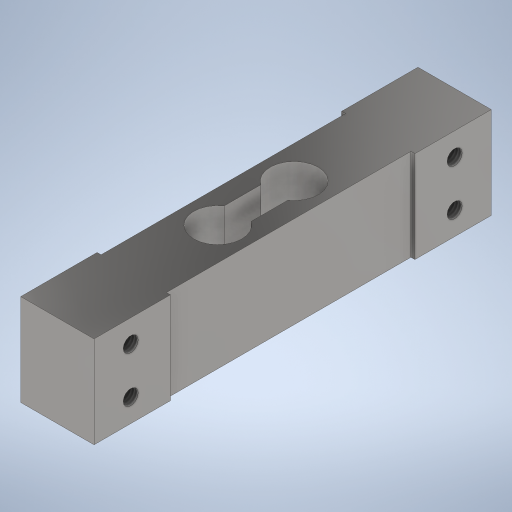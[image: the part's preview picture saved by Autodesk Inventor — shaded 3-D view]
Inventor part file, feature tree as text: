
AUTODESK INVENTOR PART (.ipt)
format: ipt  version: 2023.2 (Build 272271030, 271C)  size: 306,176 bytes
history: native  units: mm
features: sketch x2, other x1, extrude x1, hole x1
ambient origin geometry x8: Origin, YZ Plane, XZ Plane, XY Plane, X Axis, Y Axis, Z Axis, Center Point
bodies: Body1 (feature_tree)
feature tree (5):
  other  "Sólido1"
  extrude  "Extrusão1"  Depth=130.0mm
  hole  "Furo1"  [1 undecoded]
  sketch  "Esboço1"  dims[d0=24.0mm d1=130.0mm]
  sketch  "Esboço2"  dims[d2=15.7mm d3=12.0mm d4=12.0mm d5=52.5mm d6=52.5mm d8=0.0mm d9=1.3mm d10=80.0mm d11=1.3mm d12=80.0mm d13=0.0mm d14=0.0mm d15=0.0mm d16=0.0mm d17=30.0mm d18=0.0mm d19=12.0mm d20=12.0mm d21=12.0mm d22=12.0mm d23=7.5mm d24=7.5mm d25=7.5mm d26=7.5mm d27=4.917mm d28=12.0mm d29=4.0mm d30=2.0mm d31=90.0deg d32=17.1mm d33=20.594885mm d34=8.8mm d36=0.0mm d37=0.0mm d38=4.4mm d35=1.0mm d39=0.375mm d40=14.3117mm d41=0.75mm d42=20.594885mm d43=0.0625mm d44=0.75mm d45=0.375mm]
note: 1 required parameter value undecoded (feature->parameter linkage not recoverable at this tier; creation-order binding heuristic only, values carry confidence <= 0.55)
